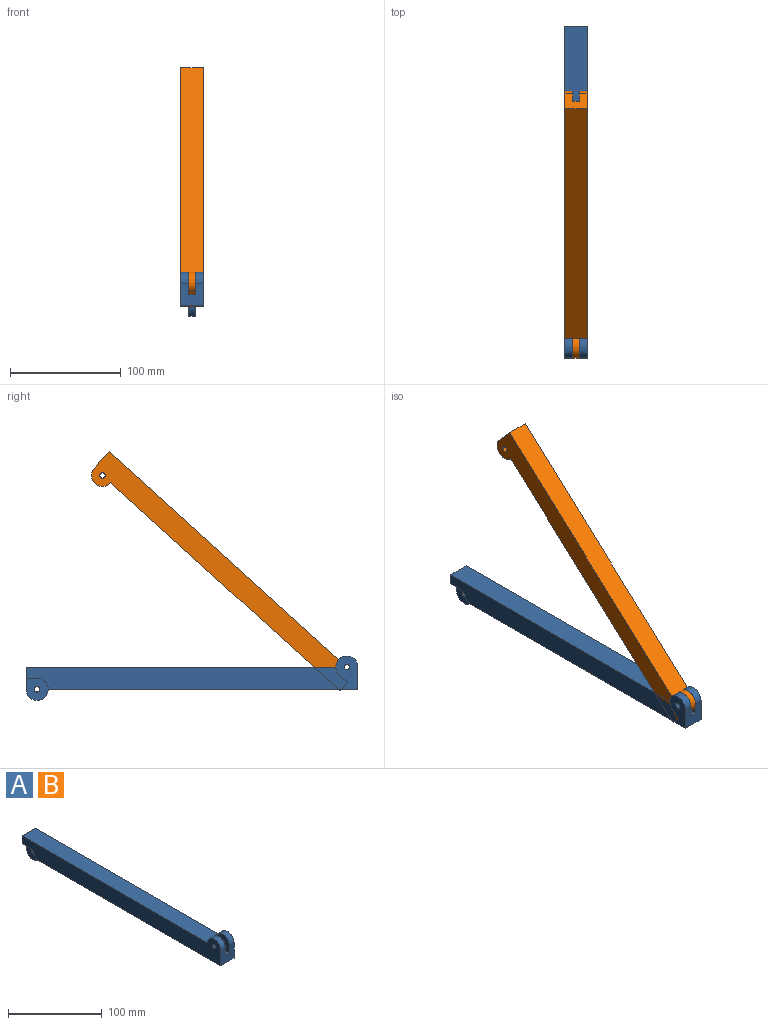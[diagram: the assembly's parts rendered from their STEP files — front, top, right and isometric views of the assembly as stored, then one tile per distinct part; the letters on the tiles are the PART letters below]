
ASSEMBLY  parts=2 mates=1
PART A: 22 faces, bbox 20x300x40 mm
  f0: plane 280x20mm, normal (0,0,1), area 5600mm2, adj f3,f4,f6,f9,f10,f21
  f1: plane 20x20mm, normal (0,-1,0), area 340mm2, adj f3,f4,f5,f7,f8,f9,f10,f20
  f2: cylinder r=2.5mm len=7mm, axis (1,0,0), area 110mm2, adj f4,f7
  f3: plane 300x30mm, normal (1,0,0), area 5958.9mm2, adj f0,f1,f5,f6,f9,f11,f16,f19
  f4: plane 300x30mm, normal (-1,0,0), area 5958.9mm2, adj f0,f1,f2,f5,f6,f10,f15,f18
  f5: plane 280x20mm, normal (0,0,-1), area 5600mm2, adj f1,f3,f4,f14,f18,f19
  f6: plane 20x20mm, normal (0,1,0), area 260mm2, adj f0,f3,f4,f12,f13,f14,f15,f16
  f7: plane 20x20mm, normal (1,0,0), area 316mm2, adj f1,f2,f10,f20,f21
  f8: plane 20x20mm, normal (-1,0,0), area 316mm2, adj f1,f9,f11,f20,f21
  f9: cylinder r=10mm len=20mm, axis (-1,0,0), area 219.9mm2, adj f0,f1,f3,f8
  f10: cylinder r=10mm len=20mm, axis (-1,0,0), area 219.9mm2, adj f0,f1,f4,f7
  f11: cylinder r=2.5mm len=7mm, axis (1,0,0), area 110mm2, adj f3,f8
  f12: plane 20x20mm, normal (1,0,0), area 316mm2, adj f6,f14,f16,f17,f19
  f13: plane 20x20mm, normal (-1,0,0), area 316mm2, adj f6,f14,f15,f17,f18
  f14: cylinder r=10mm len=20mm, axis (1,0,0), area 188.5mm2, adj f5,f6,f12,f13
  f15: plane 10x7mm, normal (0,0,-1), area 70mm2, adj f4,f6,f13,f18
  f16: plane 10x7mm, normal (0,0,-1), area 70mm2, adj f3,f6,f12,f19
  f17: cylinder r=2.5mm len=6mm, axis (-1,0,0), area 94.2mm2, adj f12,f13
  f18: cylinder r=10mm len=10mm, axis (-1,0,0), area 110mm2, adj f4,f5,f13,f15
  f19: cylinder r=10mm len=10mm, axis (-1,0,0), area 110mm2, adj f3,f5,f12,f16
  f20: plane 10x6mm, normal (0,0,1), area 60mm2, adj f1,f7,f8,f21
  f21: cylinder r=10mm len=10mm, axis (-1,0,0), area 94.2mm2, adj f0,f7,f8,f20
PART B: same geometry as A
PLACE A t=(-0.68,150.38,1.15)mm fixed
PLACE B rot(axis=(-1,0,0),137.8deg) t=(-0.68,-140.32,-2.98)mm
MATE revolute B.f14 <-> A.f9  axis (-1,0,0) through (2.32,-139.62,11.15)mm
